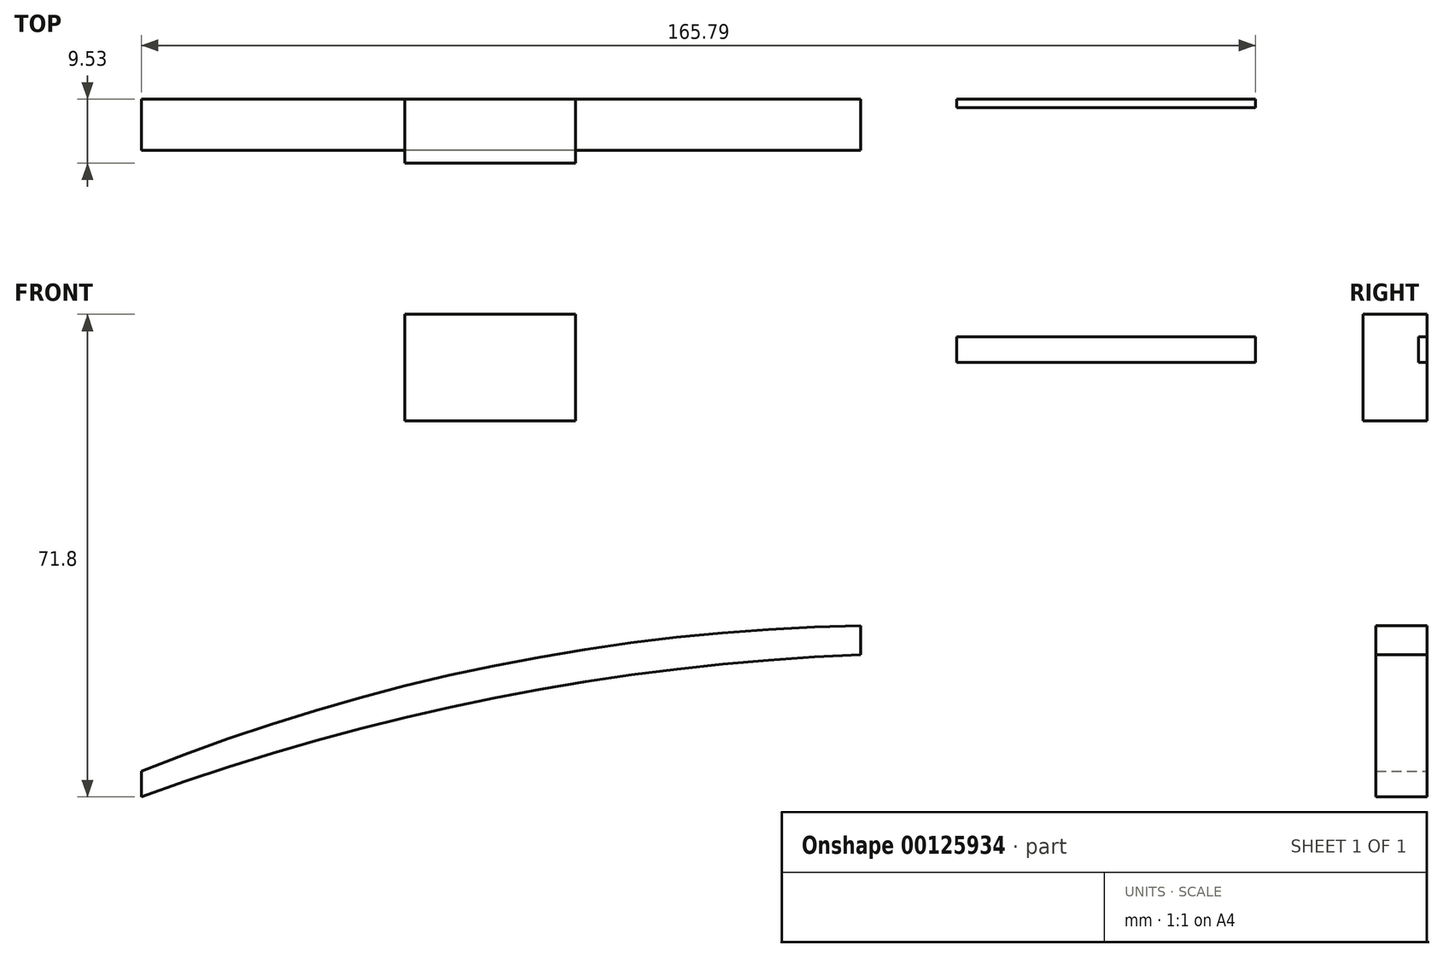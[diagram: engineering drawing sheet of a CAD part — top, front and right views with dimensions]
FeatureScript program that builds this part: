
annotation { "Feature Type Name" : "Feature", "Feature Type Description" : "" }
export const myFeature = defineFeature(function(context is Context, id is Id, definition is map)
    precondition{}
    {
        {
            var Q0;
            Q0=qCreatedBy(makeId("Front.planeOp"),FACE);
            var sketch = newSketch(context, id + "F0", { "sketchPlane" : qUnion([Q0])});
            skLineSegment(sketch, "E0.bottom", {"start": v(-55.64, 32.83) * mm, "end": v(-30.24, 32.83) * mm});
            skLineSegment(sketch, "E0.top", {"start": v(-55.64, 16.96) * mm, "end": v(-30.24, 16.96) * mm});
            skLineSegment(sketch, "E0.left", {"start": v(-55.64, 32.83) * mm, "end": v(-55.64, 16.96) * mm});
            skLineSegment(sketch, "E0.right", {"start": v(-30.24, 32.83) * mm, "end": v(-30.24, 16.96) * mm});
            skSolve(sketch);
        }
        {
            var Q0;
            Q0=qSketchRegion(id+"F0",true);
            extrude(context, id + "F1", {"entities" : qUnion([Q0]), "depth" : 9.52 * mm});
        }
        {
            var Q0;
            Q0=qCreatedBy(makeId("Front.planeOp"),FACE);
            var sketch = newSketch(context, id + "F2", { "sketchPlane" : qUnion([Q0])});
            skLineSegment(sketch, "E1.bottom", {"start": v(26.5, 29.5) * mm, "end": v(70.94, 29.5) * mm});
            skLineSegment(sketch, "E1.top", {"start": v(26.5, 25.7) * mm, "end": v(70.94, 25.7) * mm});
            skLineSegment(sketch, "E1.left", {"start": v(26.5, 29.5) * mm, "end": v(26.5, 25.7) * mm});
            skLineSegment(sketch, "E1.right", {"start": v(70.94, 29.5) * mm, "end": v(70.94, 25.7) * mm});
            skSolve(sketch);
        }
        {
            var Q0;
            Q0=qSketchRegion(id+"F2",true);
            extrude(context, id + "F3", {"entities" : qUnion([Q0]), "depth" : 1.27 * mm});
        }
        {
            var Q0;
            Q0=qCreatedBy(makeId("Front.planeOp"),FACE);
            var sketch = newSketch(context, id + "F4", { "sketchPlane" : qUnion([Q0])});
            skLineSegment(sketch, "E2", {"start": v(-94.85, -38.97) * mm, "end": v(-94.85, -35.16) * mm});
            skLineSegment(sketch, "E3", {"start": v(12.18, -13.5) * mm, "end": v(12.18, -17.8) * mm});
            skArc(sketch, "E4.trimOffspring", {"start": v(12.18, -13.5) * mm, "mid": v(-42.32, -19.46) * mm, "end": v(-94.85, -35.16) * mm});
            skArc(sketch, "E5", {"start": v(12.18, -17.8) * mm, "mid": v(-42.16, -24.23) * mm, "end": v(-94.85, -38.97) * mm});
            skSolve(sketch);
        }
        {
            var Q0;
            Q0=qSketchRegion(id+"F4",true);
            extrude(context, id + "F5", {"entities" : qUnion([Q0]), "depth" : 7.62 * mm});
        }
    });
